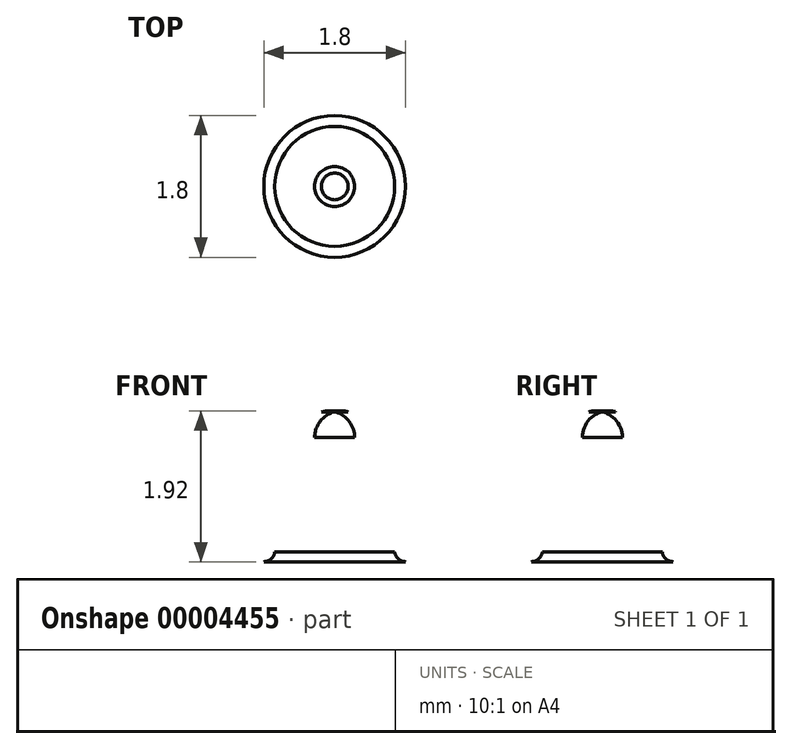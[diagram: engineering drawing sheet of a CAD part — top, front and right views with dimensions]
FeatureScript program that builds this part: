
annotation { "Feature Type Name" : "Feature", "Feature Type Description" : "" }
export const myFeature = defineFeature(function(context is Context, id is Id, definition is map)
    precondition{}
    {
        {
            var Q0;
            Q0=qCreatedBy(makeId("Front.planeOp"),FACE);
            var sketch = newSketch(context, id + "F0", { "sketchPlane" : qUnion([Q0])});
            skLineSegment(sketch, "E0", {"start": v(0, 0) * mm, "end": v(0, 1.78) * mm});
            skLineSegment(sketch, "E1", {"start": v(-0.76, 0) * mm, "end": v(0, 0) * mm});
            skArc(sketch, "E2", {"start": v(0, 1.78) * mm, "mid": v(-0.53, 0.95) * mm, "end": v(-0.76, 0) * mm});
            skLineSegment(sketch, "E3.bottom", {"start": v(0, 1.78) * mm, "end": v(-0.25, 1.78) * mm});
            skLineSegment(sketch, "E3.top", {"start": v(0, 1.45) * mm, "end": v(-0.25, 1.45) * mm});
            skLineSegment(sketch, "E3.left", {"start": v(0, 1.78) * mm, "end": v(0, 1.45) * mm});
            skLineSegment(sketch, "E3.right", {"start": v(-0.25, 1.78) * mm, "end": v(-0.25, 1.45) * mm});
            skArc(sketch, "E4", {"start": v(0, 1.78) * mm, "mid": v(-0.18, 1.66) * mm, "end": v(-0.25, 1.45) * mm});
            skArc(sketch, "E5", {"start": v(-0.76, 0) * mm, "mid": v(-0.8, -0.1) * mm, "end": v(-0.9, -0.13) * mm});
            skLineSegment(sketch, "E6", {"start": v(-0.9, -0.13) * mm, "end": v(0, -0.13) * mm});
            skLineSegment(sketch, "E7", {"start": v(0, -0.13) * mm, "end": v(0, 0) * mm});
            skSolve(sketch);
        }
        {
            var Q0;
            Q0=makeQuery(id+"F0.imprint","IMPRINT",FACE,{"disambiguationData":[TD([[makeQuery(id+"F0.imprint","IMPRINT",EDGE,{"derivedFrom":sQuery(id+"F0.wireOp",EDGE,"E0")}),1.0]])]});
            var Q1;
            {var subQ1=sQuery(id+"F0.wireOp",EDGE,"E3.top");Q1=makeQuery(id+"F0.imprint","IMPRINT",FACE,{"disambiguationData":[TD([[makeQuery(id+"F0.imprint","IMPRINT",EDGE,{"derivedFrom":subQ1}),-1.0]])]});}
            var Q2;
            {var subQ0=sQuery(id+"F0.wireOp",EDGE,"E4");Q2=makeQuery(id+"F0.imprint","IMPRINT",FACE,{"disambiguationData":[TD([[makeQuery(id+"F0.imprint","IMPRINT",EDGE,{"derivedFrom":subQ0}),1.0]])]});}
            var Q3;
            Q3=makeQuery(id+"F0.imprint","IMPRINT",FACE,{"disambiguationData":[TD([[makeQuery(id+"F0.imprint","IMPRINT",EDGE,{"derivedFrom":sQuery(id+"F0.wireOp",EDGE,"E1")}),-1.0]])]});
            var Q4;
            Q4=sQuery(id+"F0.wireOp",EDGE,"E0");
            revolve(context, id + "F1", {"entities" : qUnion([Q0, Q1, Q2, Q3]), "axis" : qUnion([Q4]), "revolveType" : RevolveType.FULL});
        }
    });
